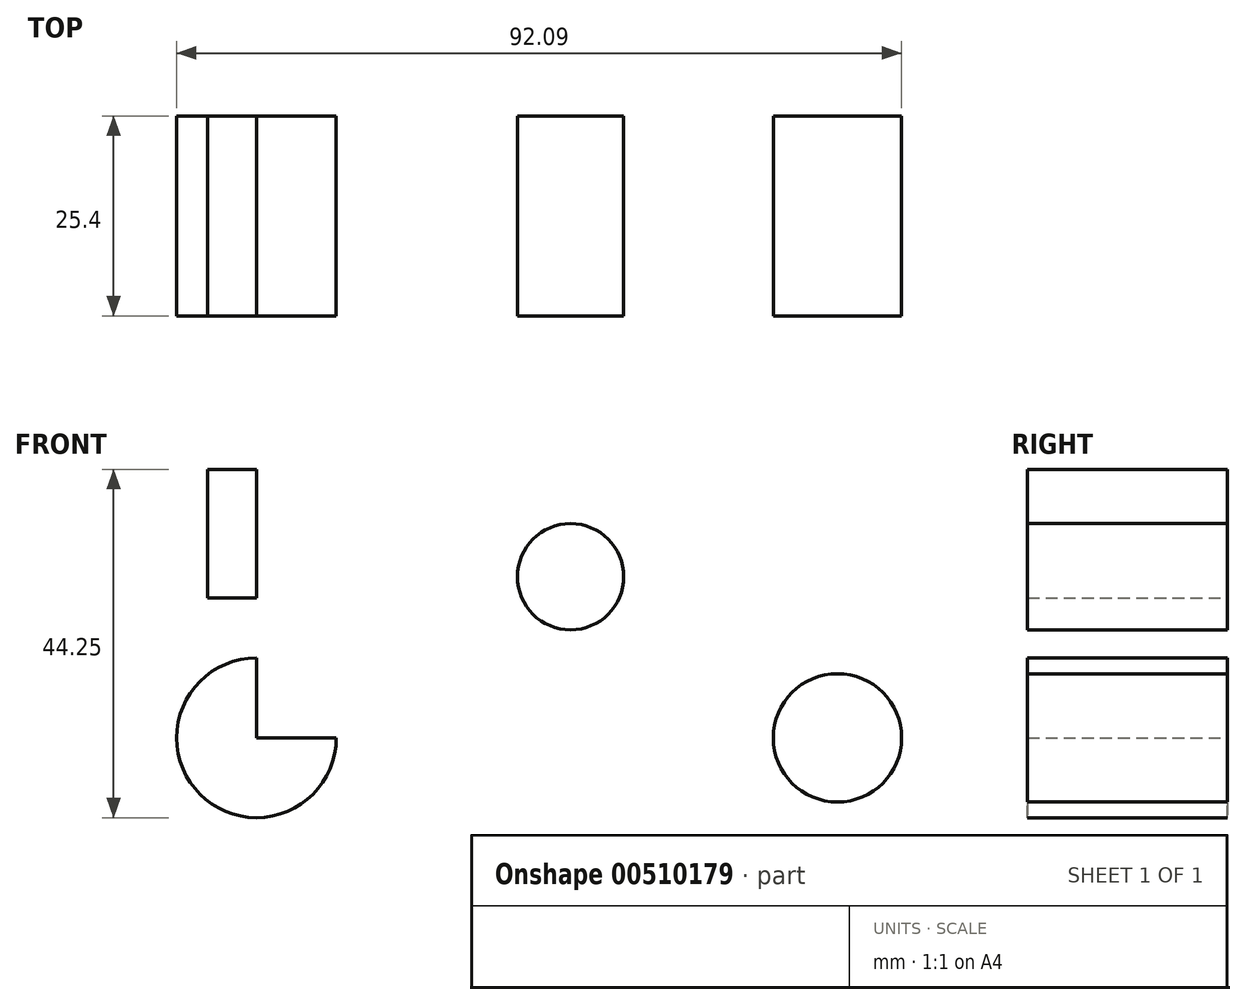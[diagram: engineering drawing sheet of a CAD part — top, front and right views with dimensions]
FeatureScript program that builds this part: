
annotation { "Feature Type Name" : "Feature", "Feature Type Description" : "" }
export const myFeature = defineFeature(function(context is Context, id is Id, definition is map)
    precondition{}
    {
        {
            var Q0;
            Q0=qCreatedBy(makeId("Front.planeOp"),FACE);
            var sketch = newSketch(context, id + "F0", { "sketchPlane" : qUnion([Q0])});
            skLineSegment(sketch, "E0", {"start": v(-59.96, 41.35) * mm, "end": v(-59.96, 2.27) * mm});
            skLineSegment(sketch, "E1", {"start": v(-59.96, 2.27) * mm, "end": v(21.09, 2.27) * mm});
            skLineSegment(sketch, "E2", {"start": v(0, 2.27) * mm, "end": v(-20.05, 22.74) * mm});
            skCircle(sketch, "E3", {"center": v(-20.05, 22.74) * mm, "radius": 6.75 * mm});
            skCircle(sketch, "E4", {"center": v(13.85, 2.27) * mm, "radius": 8.15 * mm});
            skCircle(sketch, "E5", {"center": v(-59.96, 2.27) * mm, "radius": 10.14 * mm});
            skLineSegment(sketch, "E6.bottom", {"start": v(-59.96, 20.05) * mm, "end": v(-66.16, 20.05) * mm});
            skLineSegment(sketch, "E6.top", {"start": v(-59.96, 36.39) * mm, "end": v(-66.16, 36.39) * mm});
            skLineSegment(sketch, "E6.left", {"start": v(-59.96, 20.05) * mm, "end": v(-59.96, 36.39) * mm});
            skLineSegment(sketch, "E6.right", {"start": v(-66.16, 20.05) * mm, "end": v(-66.16, 36.39) * mm});
            skSolve(sketch);
        }
        {
            var Q0;
            {var subQ0=sQuery(id+"F0.wireOp",EDGE,"E1");var subQ1=sQuery(id+"F0.wireOp",EDGE,"E0");var subQ2=makeQuery(id+"F0.imprint","INTERSECT",VERTEX,{"derivedFrom":[subQ1,subQ0]});Q0=makeQuery(id+"F0.imprint","IMPRINT",FACE,{"disambiguationData":[TD([[makeQuery(id+"F0.imprint","IMPRINT",EDGE,{"disambiguationData":[TD([[subQ2,1.0]])],"derivedFrom":subQ1}),-1.0]])]});}
            var Q1;
            Q1=makeQuery(id+"F0.imprint","IMPRINT",FACE,{"disambiguationData":[TD([[makeQuery(id+"F0.imprint","IMPRINT",EDGE,{"derivedFrom":sQuery(id+"F0.wireOp",EDGE,"E6.bottom")}),-1.0]])]});
            var Q2;
            Q2=makeQuery(id+"F0.imprint","IMPRINT",FACE,{"disambiguationData":[TD([[makeQuery(id+"F0.imprint","IMPRINT",EDGE,{"derivedFrom":sQuery(id+"F0.wireOp",EDGE,"E4")}),1.0]])]});
            var Q3;
            Q3=makeQuery(id+"F0.imprint","IMPRINT",FACE,{"disambiguationData":[TD([[makeQuery(id+"F0.imprint","IMPRINT",EDGE,{"derivedFrom":sQuery(id+"F0.wireOp",EDGE,"E3")}),1.0]])]});
            extrude(context, id + "F1", {"entities" : qUnion([Q0, Q1, Q2, Q3]), "depth" : 25.4 * mm, "offsetDistance" : 25.4 * mm});
        }
    });
